# Revit family: Nuaire_IfcFanType_EsOpusdc
name_source: partatom
category: Mechanical Equipment
revit_build: Autodesk Revit 2018 (Build: 20170223_1515(x64)
units: mm (PartAtom-declared; Revit-internal decimal feet)

## family parameters
Always vertical = No
Cut with Voids When Loaded = No
OmniClass Number = 23.75.00.00
OmniClass Title = Climate Control (HVAC)
Part Type = Normal
Room Calculation Point = No
Round Connector Dimension = Use Radius
Shared = No
Work Plane-Based = Yes

## types (6) — shared parameters
6 Monthly = SFG20 20-03
Access Clearance Bottom = 184 mm  [stored 0.603675 ft]
Annually = SFG20 20-03
BMS Links = Yes
Battery Supply = No
CE Approval = Yes
COBie.Type = Yes
COBie.Type.Length = 242 mm  [stored 0.793963 ft]
COBie.Type.Manufacturer = Nuaire
COBie.Type.NominalHeight = 184 mm  [stored 0.603675 ft]
COBie.Type.NominalLength = 242 mm  [stored 0.793963 ft]
COBie.Type.NominalWidth = 367 mm  [stored 1.20407 ft]
COBie.Type.WarrantyDescription = 5 years. First year parts and labour, remaining 4 years parts only.
COBie.Type.WarrantyDurationLabor = 1
COBie.Type.WarrantyDurationParts = 5
COBie.Type.WarrantyDurationUnit = Year
COBie.Type.WarrantyGuarantorLabor = Nuaire
COBie.Type.WarrantyGuarantorParts = Nuaire
Catalogue Pages = http://www.nuaire.info
Daily = SFG20 20-03
Default Elevation = 1219 mm
Environmental Product Declaration = WEEE, RoHS
Fax Number = +44(0)2920-858-222
Fire Control Panel Links = No
Frequency = 50 Hz
Height = 184 mm  [stored 0.603675 ft]
I&M Manual = http://www.nuaire.info
IFCExportAs = IfcFanType
Length = 242 mm  [stored 0.793963 ft]
Location of Manufacturer = 51.571856, -3.232638
Maintenance Required 0 to 300hrs = http://www.nuaire.info
Maintenance Required 1001 to 2000hrs = http://www.nuaire.info
Maintenance Required 2001 to 4000hrs = http://www.nuaire.info
Maintenance Required 301 to 600hrs = http://www.nuaire.info
Maintenance Required 4001 to 8000hrs = http://www.nuaire.info
Maintenance Required 601 to 1000hrs = http://www.nuaire.info
Maintenance Required 8001 to 12000hrs = http://www.nuaire.info
Manufacturer = Nuaire
Manufacturer Website = http://www.nuaire.co.uk
Maximum Ambient Temperature = 40 °C
Monthly = SFG20 20-03
Number of Connection Poles = 2
OmniClass Number = 23-33 31 19 13
OmniClass Title = Centrifugal Fans
Operation and Maintenance Manual = http://www.nuaire.info
Postcode = CF83 1NA
Power Source = Mains
Product Literature = http://www.nuaire.info
Product Range = Opus DC
Quarterly = SFG20 20-03
Reference Standard = BS EN 60335-2-80
Responsible Sourcing of Materials = FSC
Revit Family Last Revised = 2020-09-23T15:04:00
Spigot Diameter = 100 mm  [stored 0.328084 ft]
Spigot Radius = 50 mm  [stored 0.164042 ft]
Supply Phase = 1
Telephone Number = +44(0)2920-858-200
Template Custodian = Nuaire
URL = http://www.nuaire.co.uk
Voltage = 230 V
Weatherproof or Internal Only = Internal Only
Weekly = SFG20 20-03
Weight = 3.00 kg
Width = 367 mm  [stored 1.20407 ft]
zero-valued in all types: COBie.Type.ReplacementCost, Life Cycle Analysis

## per-type parameters (varying)
| type | Apparent Load | COBie.Type.Category | COBie.Type.Description | Classification System | Classification.Uniclass.Pr.Description | Classification.Uniclass.Pr.Number | Description | Full Load Current | IFCExportType | Nominal Motor Rating | Starting Current | Suitability for Use |
| ES-OPUSDC110-M | 106 VA | Pr_65_67_29_12 : Centrifugal fans | Inline Extract Dual Fan | Uniclass2015 | Centrifugal fans | Pr_65_67_29_12 | Inline Extract Dual Fan | 0.46 A | CENTRIFUGALFORWARDCURVED | 0.090 kW | 0.61 A | Approved |
| ES-OPUSDC75-M | 69 VA | Pr_65_67_29_12 : Centrifugal fans | Inline Extract Dual Fan |  | Centrifugal fans | Pr_65_67_29_12 | Inline Extract Dual Fan | 0.30 A |  | 0.033 kW | 0.35 A |  |
| ES-OPUSDC60-2M | 74 VA | Pr_65_67_29_89 : Twin centrifugal fans | Inline Extract Twin Fan |  | Twin centrifugal fans | Pr_65_67_29_89 | Inline Extract Twin Fan | 0.32 A |  | 0.044 kW | 0.40 A |  |
| ES-OPUSDC60-M | 74 VA | Pr_65_67_29_12 : Centrifugal fans | Inline Extract Single Fan |  | Centrifugal fans | Pr_65_67_29_12 | Inline Extract Single Fan | 0.32 A |  | 0.044 kW | 0.40 A |  |
| ES-OPUSDC40-2M | 32 VA | Pr_65_67_29_89 : Twin centrifugal fans | Inline Extract Twin Fan |  | Twin centrifugal fans | Pr_65_67_29_89 | Inline Extract Twin Fan | 0.14 A |  | 0.018 kW | 0.18 A |  |
| ES-OPUSDC40-M | 32 VA | Pr_65_67_29_12 : Centrifugal fans | Inline Extract Single Fan |  | Centrifugal fans | Pr_65_67_29_12 | Inline Extract Single Fan | 0.14 A |  | 0.018 kW | 0.18 A |  |

note: column(s) folded — value = type name in every type: COBie.Type.ModelNumber, COBie.Type.Name, Model

note: [stored X ft] marks values corroborated as IEEE doubles in the binary element streams (Revit-internal decimal feet)

## geometry (parser evidence)
native form markers: Sweep x14
no freeform markers — native parametric forms only
